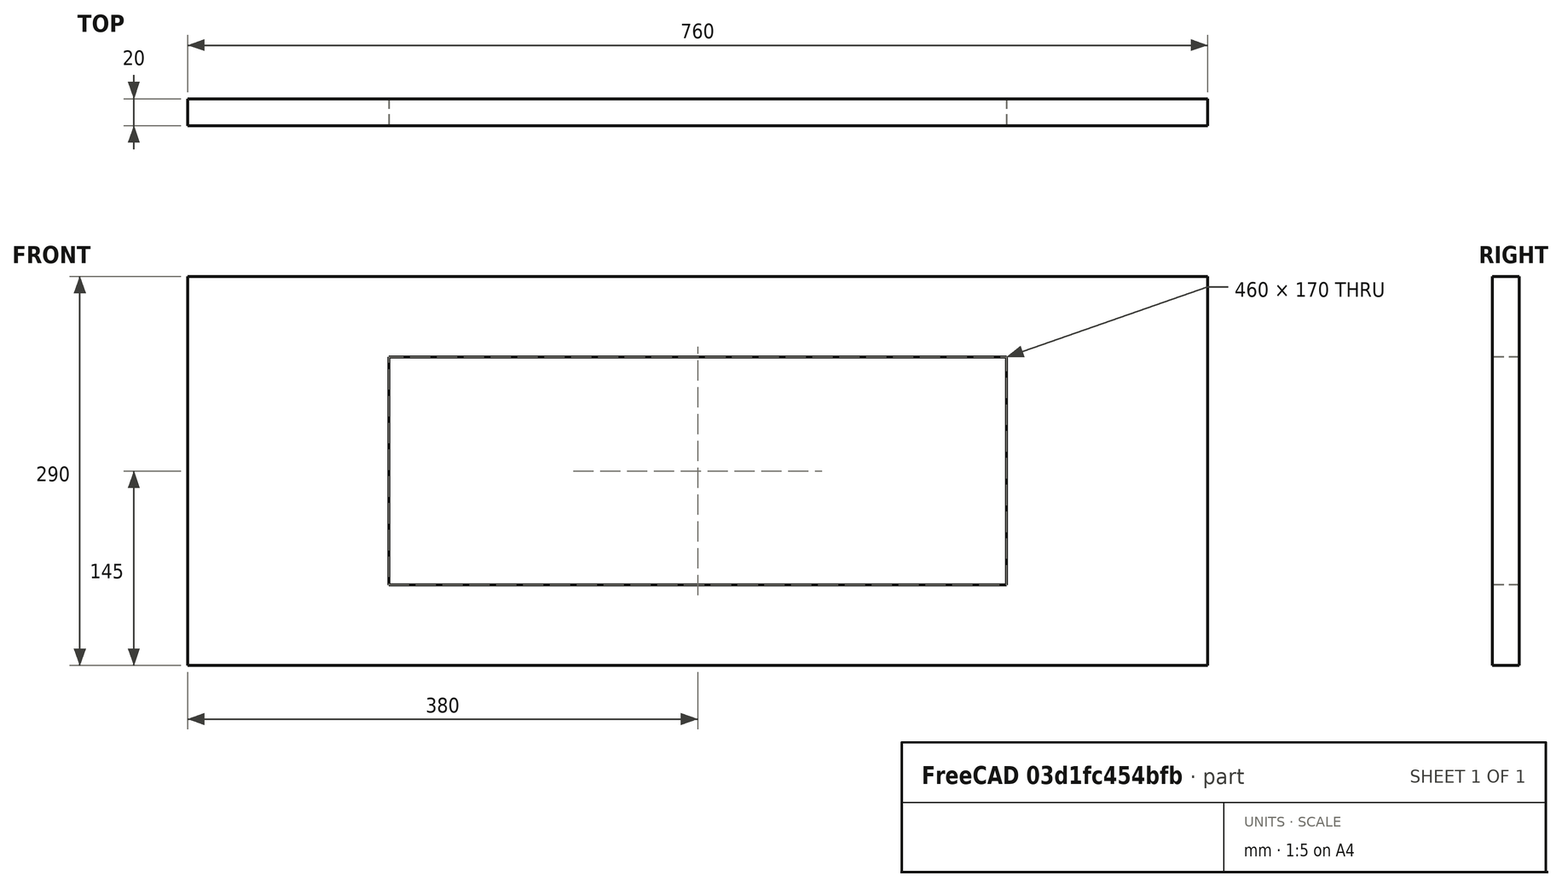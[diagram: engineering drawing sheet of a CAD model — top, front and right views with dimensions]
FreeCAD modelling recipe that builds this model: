
FCSTD DOCUMENT  (FreeCAD 0.20R29603 (Git))
Label: RegalBlende
License: All rights reserved
LicenseURL: http://en.wikipedia.org/wiki/All_rights_reserved
objects: Sketcher::SketchObject×1, PartDesign::Pad×1, PartDesign::Body×1
note: 4 computed .brp shape members not serialized (recipe doc carries the construction recipe); baked Part::Feature solids carry a one-line shape summary decoded from their .brp

FEATURE [Sketcher::SketchObject] Sketch
  FullyConstrained = true
  MapMode = 5
  Placement = pos=(0,0,0) rot=(1,0,0;1.5708rad)
  Support = -> [XZ_Plane]
  sketch-geometry (8):
    g0: LineSegment StartX=-380 StartY=0 StartZ=0 EndX=380 EndY=0 EndZ=0
    g1: LineSegment StartX=380 StartY=0 StartZ=0 EndX=380 EndY=290 EndZ=0
    g2: LineSegment StartX=380 StartY=290 StartZ=0 EndX=-380 EndY=290 EndZ=0
    g3: LineSegment StartX=-380 StartY=290 StartZ=0 EndX=-380 EndY=0 EndZ=0
    g4: LineSegment StartX=-230 StartY=230 StartZ=0 EndX=230 EndY=230 EndZ=0
    g5: LineSegment StartX=230 StartY=230 StartZ=0 EndX=230 EndY=60 EndZ=0
    g6: LineSegment StartX=230 StartY=60 StartZ=0 EndX=-230 EndY=60 EndZ=0
    g7: LineSegment StartX=-230 StartY=60 StartZ=0 EndX=-230 EndY=230 EndZ=0
  constraints (22):
    c: Coincident(g0,g1)
    c: Coincident(g1,g2)
    c: Coincident(g2,g3)
    c: Coincident(g3,g0)
    c: Horizontal(g2)
    c: Vertical(g1)
    c: Vertical(g3)
    c: PointOnObject(g0,g-1)
    c: Distance(g2) = 760
    c: Distance(g3) = 290
    c: Symmetric(g0,g0,g-2)
    c: Coincident(g4,g5)
    c: Coincident(g5,g6)
    c: Coincident(g6,g7)
    c: Coincident(g7,g4)
    c: Horizontal(g4)
    c: Vertical(g5)
    c: Vertical(g7)
    c: Symmetric(g6,g5,g-2)
    c: Distance(g5,g0) = 60
    c: Distance(g4,g2) = 60
    c: Distance(g5,g1) = 150
FEATURE [PartDesign::Pad] Pad
  Direction = (0,-1,2e-16)
  Length = 20
  Length2 = 10
  Placement = pos=(0,0,0) rot=(1,0,0;1.5708rad)
  Profile = -> Sketch
  ReferenceAxis = -> Sketch [N_Axis]
  Type = 0
FEATURE [PartDesign::Body] Body
  Group = -> [Sketch,Pad]
  Origin = -> Origin
  Tip = -> Pad
